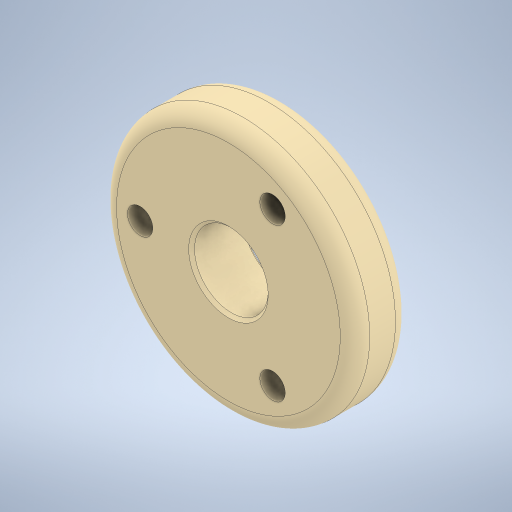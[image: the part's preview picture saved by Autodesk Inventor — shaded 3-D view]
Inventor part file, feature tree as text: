
AUTODESK INVENTOR PART (.ipt)
format: ipt  version: 2024 (Build 280153000, 153)  size: 285,696 bytes
history: native  units: in
note: dims shown in document units (in); Inventor stores cm internally (conversion verified against a paired STEP export)
features: extrude x2, sketch x2, fillet x1, chamfer x1, plane x1, pattern_circular x1, direct_edit x1, other x1
ambient origin geometry x8: Origin, YZ Plane, XZ Plane, XY Plane, X Axis, Y Axis, Z Axis, Center Point
bodies: Solid1 (feature_tree)
feature tree (10):
  extrude  "Extrusion1"  Depth=0.43in
  fillet  "Fillet1"  Radius=0.0938in
  chamfer  "Chamfer1"  Distance=0.005in Angle=45.0deg
  plane  "Work Plane1"
  extrude  "Extrusion2"  TaperAngle=0.0deg  [1 undecoded]
  pattern_circular  "Circular Pattern1"  [2 undecoded]
  direct_edit  "Direct Edit1"
  sketch  "Sketch1"  dims[d0=0.125in d1=0.43in d2=0.0938in d3=0.0in]
  sketch  "Sketch2"  dims[d4=0.025in d5=0.005in d6=0.125in d7=45.0deg d8=0.0in d9=0.043in d10=0.15in d11=0.0938in d12=0.0in d13=1.1811in d14=360.0deg d16=3.937in d17=0.3937in d18=0.3937in]
  other  "Scale1"
note: 3 required parameter values undecoded (feature->parameter linkage not recoverable at this tier; creation-order binding heuristic only, values carry confidence <= 0.55)
